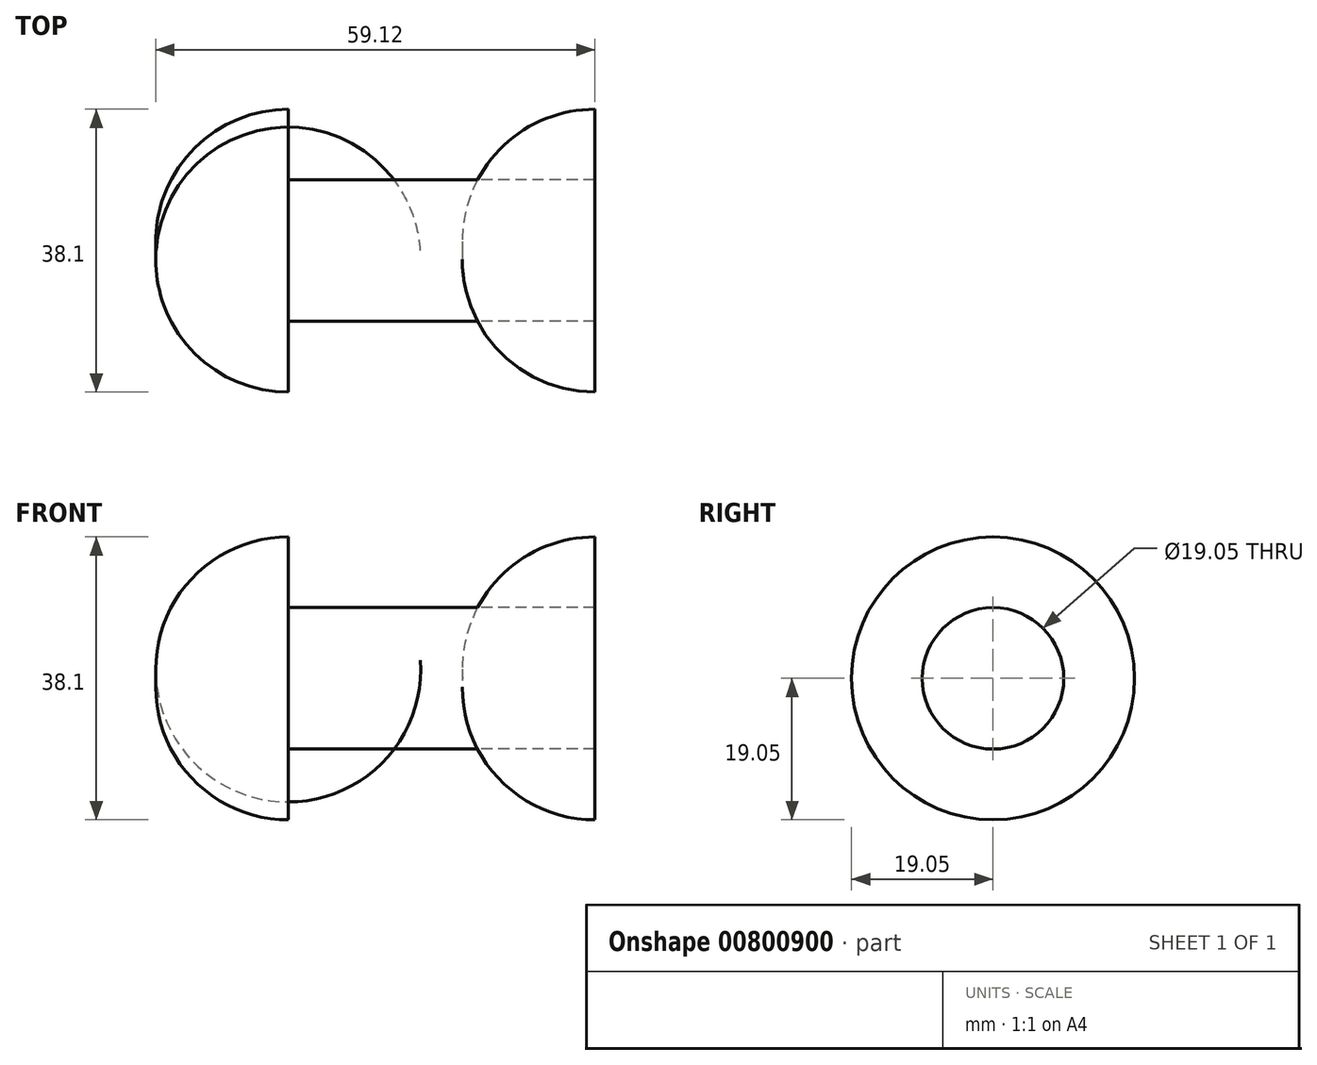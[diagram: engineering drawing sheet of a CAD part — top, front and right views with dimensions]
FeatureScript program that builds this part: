
annotation { "Feature Type Name" : "Feature", "Feature Type Description" : "" }
export const myFeature = defineFeature(function(context is Context, id is Id, definition is map)
    precondition{}
    {
        {
            var Q0;
            Q0=qCreatedBy(makeId("Front.planeOp"),FACE);
            var sketch = newSketch(context, id + "F0", { "sketchPlane" : qUnion([Q0])});
            skLineSegment(sketch, "E0", {"start": v(-20.64, 19.05) * mm, "end": v(-20.64, 9.52) * mm});
            skLineSegment(sketch, "E1", {"start": v(-20.64, 9.52) * mm, "end": v(0, 9.52) * mm});
            skArc(sketch, "E2.trimOffspring", {"start": v(-20.64, 19.05) * mm, "mid": v(-33.67, 13.39) * mm, "end": v(-38.44, 0) * mm});
            skPoint(sketch, "E3.center.orphan", {"position": v(-37.91, 0) * mm});
            skPoint(sketch, "E4.end.orphan", {"position": v(0, 9.53) * mm});
            skLineSegment(sketch, "E5.MirrorCS", {"start": v(20.64, 9.53) * mm, "end": v(0, 9.53) * mm});
            skLineSegment(sketch, "E6.MirrorCS", {"start": v(20.64, 19.05) * mm, "end": v(20.64, 9.52) * mm});
            skArc(sketch, "E7.MirrorCS", {"start": v(20.64, 19.05) * mm, "mid": v(33.67, 13.39) * mm, "end": v(38.44, 0) * mm});
            skLineSegment(sketch, "E8", {"start": v(-38.44, 0) * mm, "end": v(38.44, 0) * mm, "construction": true});
            skLineSegment(sketch, "E9", {"start": v(-38.44, 0) * mm, "end": v(38.44, 0) * mm});
            skSolve(sketch);
        }
        {
            var Q0;
            Q0 = qSketchRegion(id + "F0", true);
            var Q1;
            Q1=sQuery(id+"F0.wireOp",EDGE,"E8");
            revolve(context, id + "F1", {"surfaceOperationType" : NewSurfaceOperationType.NEW, "entities" : qUnion([Q0]), "axis" : qUnion([Q1]), "revolveType" : RevolveType.FULL});
        }
    });
